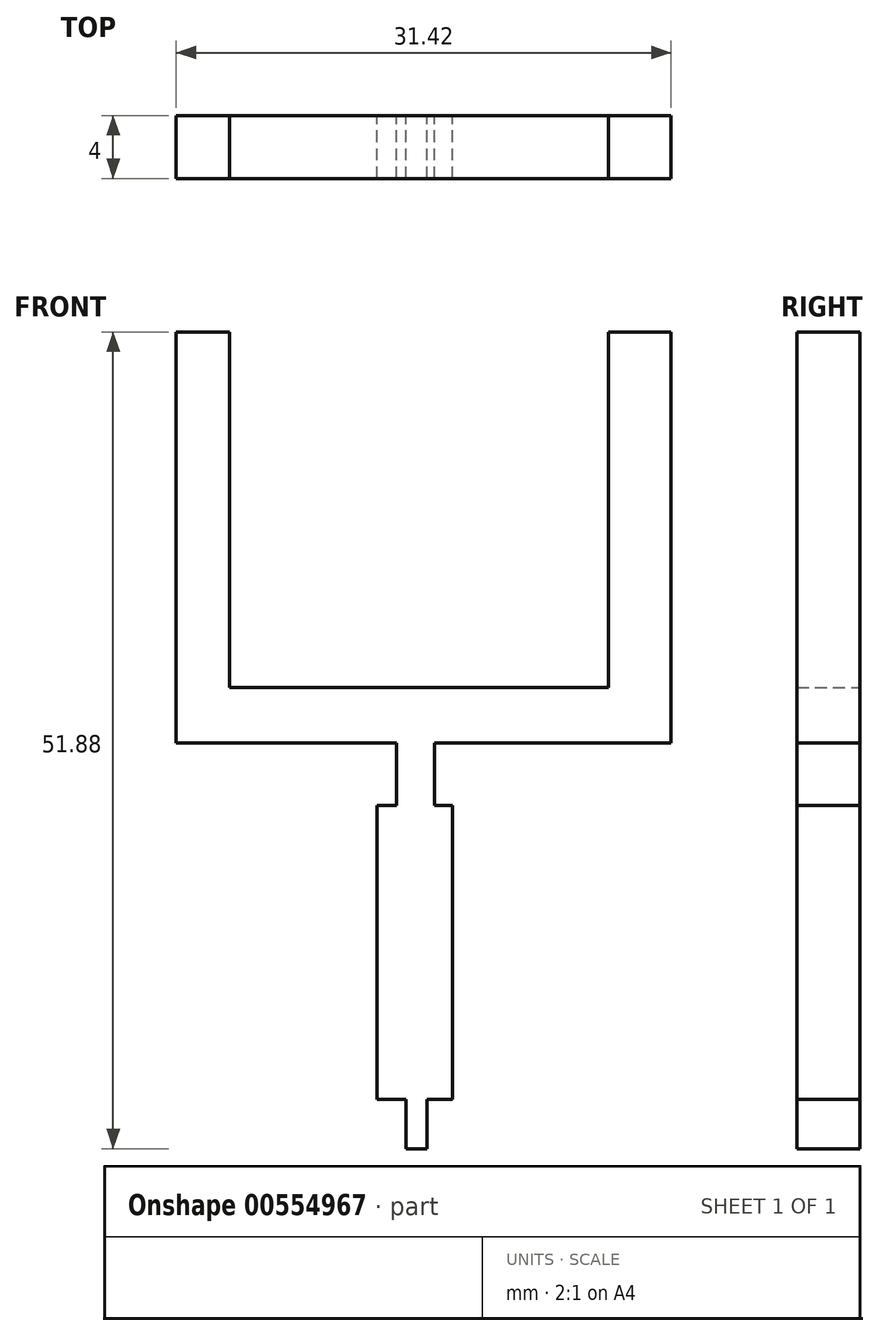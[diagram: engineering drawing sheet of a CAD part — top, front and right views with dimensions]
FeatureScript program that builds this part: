
annotation { "Feature Type Name" : "Feature", "Feature Type Description" : "" }
export const myFeature = defineFeature(function(context is Context, id is Id, definition is map)
    precondition{}
    {
        {
            var Q0;
            Q0=qCreatedBy(makeId("Front.planeOp"),FACE);
            var sketch = newSketch(context, id + "F0", { "sketchPlane" : qUnion([Q0])});
            skLineSegment(sketch, "E0", {"start": v(-49.03, 43.93) * mm, "end": v(-49.03, 17.8) * mm});
            skLineSegment(sketch, "E1", {"start": v(-49.03, 17.8) * mm, "end": v(-35.05, 17.8) * mm});
            skLineSegment(sketch, "E2", {"start": v(-35.05, 17.8) * mm, "end": v(-35.05, 13.85) * mm});
            skLineSegment(sketch, "E3", {"start": v(-35.05, 13.85) * mm, "end": v(-32.62, 13.85) * mm});
            skLineSegment(sketch, "E4", {"start": v(-32.62, 13.85) * mm, "end": v(-32.62, 17.8) * mm});
            skLineSegment(sketch, "E5", {"start": v(-32.62, 17.8) * mm, "end": v(-17.61, 17.8) * mm});
            skLineSegment(sketch, "E6", {"start": v(-17.61, 17.8) * mm, "end": v(-17.61, 43.93) * mm});
            skLineSegment(sketch, "E7", {"start": v(-17.61, 43.93) * mm, "end": v(-21.59, 43.93) * mm});
            skLineSegment(sketch, "E8", {"start": v(-21.59, 43.93) * mm, "end": v(-21.59, 21.34) * mm});
            skLineSegment(sketch, "E9", {"start": v(-21.59, 21.34) * mm, "end": v(-45.65, 21.34) * mm});
            skLineSegment(sketch, "E10", {"start": v(-45.65, 21.34) * mm, "end": v(-45.65, 43.93) * mm});
            skLineSegment(sketch, "E11", {"start": v(-45.65, 43.93) * mm, "end": v(-49.03, 43.93) * mm});
            skLineSegment(sketch, "E12", {"start": v(-35.05, 13.85) * mm, "end": v(-36.29, 13.85) * mm});
            skLineSegment(sketch, "E13", {"start": v(-36.29, 13.85) * mm, "end": v(-36.29, -4.82) * mm});
            skLineSegment(sketch, "E14", {"start": v(-36.29, -4.82) * mm, "end": v(-31.5, -4.82) * mm});
            skLineSegment(sketch, "E15", {"start": v(-31.5, -4.82) * mm, "end": v(-31.5, 13.85) * mm});
            skLineSegment(sketch, "E16", {"start": v(-31.5, 13.85) * mm, "end": v(-32.62, 13.85) * mm});
            skSolve(sketch);
        }
        {
            var Q0;
            Q0 = qSketchRegion(id + "F0", true);
            extrude(context, id + "F1", {"entities" : qUnion([Q0]), "depth" : 4 * mm, "offsetDistance" : 25 * mm});
        }
        {
            var Q0;
            Q0=qCreatedBy(makeId("Front.planeOp"),FACE);
            var sketch = newSketch(context, id + "F2", { "sketchPlane" : qUnion([Q0])});
            skLineSegment(sketch, "E17.bottom", {"start": v(-34.43, -4.7) * mm, "end": v(-33.12, -4.7) * mm});
            skLineSegment(sketch, "E17.top", {"start": v(-34.43, -7.95) * mm, "end": v(-33.12, -7.95) * mm});
            skLineSegment(sketch, "E17.left", {"start": v(-34.43, -4.7) * mm, "end": v(-34.43, -7.95) * mm});
            skLineSegment(sketch, "E17.right", {"start": v(-33.12, -4.7) * mm, "end": v(-33.12, -7.95) * mm});
            skSolve(sketch);
        }
        {
            var Q0;
            Q0 = qSketchRegion(id + "F2", true);
            extrude(context, id + "F3", {"entities" : qUnion([Q0]), "operationType" : NewBodyOperationType.ADD, "depth" : 4 * mm, "offsetDistance" : 25 * mm});
        }
    });
